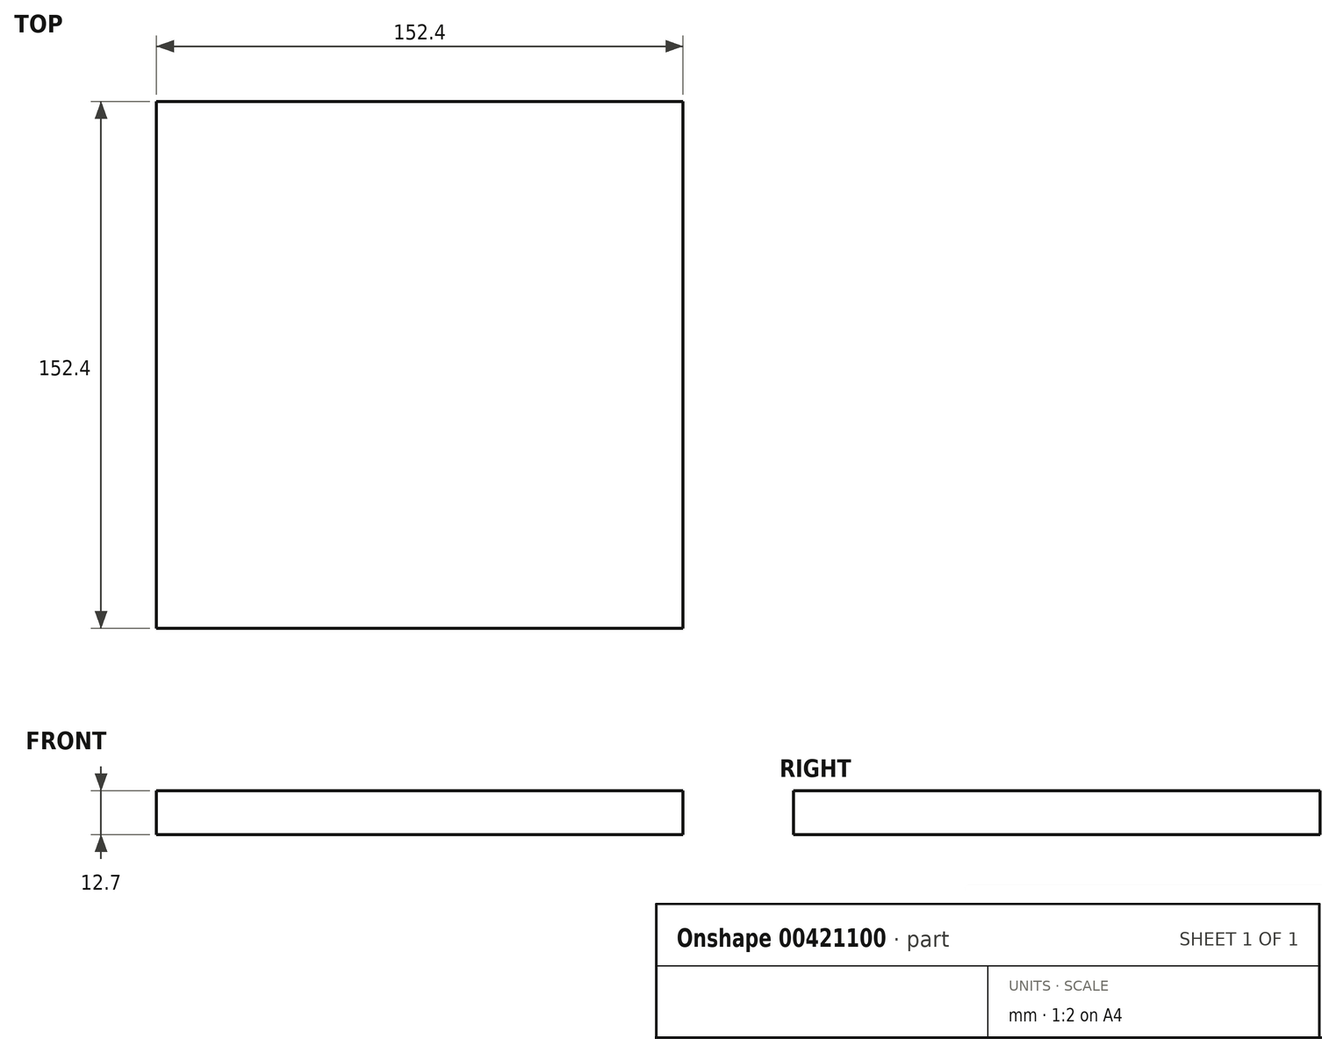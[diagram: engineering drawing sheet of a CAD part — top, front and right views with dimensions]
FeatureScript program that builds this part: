
annotation { "Feature Type Name" : "Feature", "Feature Type Description" : "" }
export const myFeature = defineFeature(function(context is Context, id is Id, definition is map)
    precondition{}
    {
        {
            var Q0;
            Q0=qCreatedBy(makeId("Top.planeOp"),FACE);
            var sketch = newSketch(context, id + "F0", { "sketchPlane" : qUnion([Q0])});
            skLineSegment(sketch, "E0.bottom", {"start": v(76.2, -76.2) * mm, "end": v(-76.2, -76.2) * mm});
            skLineSegment(sketch, "E0.top", {"start": v(76.2, 76.2) * mm, "end": v(-76.2, 76.2) * mm});
            skLineSegment(sketch, "E0.left", {"start": v(76.2, -76.2) * mm, "end": v(76.2, 76.2) * mm});
            skLineSegment(sketch, "E0.right", {"start": v(-76.2, -76.2) * mm, "end": v(-76.2, 76.2) * mm});
            skPoint(sketch, "E0.middle", {"position": v(0, 0) * mm});
            skSolve(sketch);
        }
        {
            var Q0;
            Q0 = qSketchRegion(id + "F0", true);
            extrude(context, id + "F1", {"entities" : qUnion([Q0]), "endBound" : BoundingType.SYMMETRIC, "depth" : 12.7 * mm});
        }
    });
